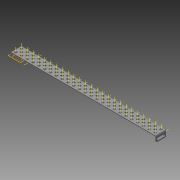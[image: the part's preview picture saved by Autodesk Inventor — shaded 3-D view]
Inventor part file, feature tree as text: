
AUTODESK INVENTOR PART (.ipt)
format: ipt  version: 2015 (Build 190159000, 159)  size: 1,080,320 bytes
history: native  units: in
note: dims shown in document units (in); Inventor stores cm internally (conversion verified against a paired STEP export)
features: other x148, pattern_linear x3, extrude x2, sketch x2, chamfer x1, imported_body x1
ambient origin geometry x8: Origin, YZ Plane, XZ Plane, XY Plane, X Axis, Y Axis, Z Axis, Center Point
bodies: Body1 (feature_tree)
feature tree (157):
  chamfer  "Chamfer2"  Distance=0.5in
  other  "Rail"
  extrude  "right end cut"  Depth=0.5in
  extrude  "length cut"  TaperAngle=0.0deg  [1 undecoded]
  other  "top axis"
  other  "inner axis"
  other  "horiz axis"
  pattern_linear  "top axes"  Count1=3 Spacing1=0.5in
  pattern_linear  "inner axes"  Spacing1=0.0in  [1 undecoded]
  pattern_linear  "horiz axes"  Spacing1=0.0in  [1 undecoded]
  other  "slot plane"
  imported_body  "Base1"
  other  "Work Point1"
  other  "Work Point2"
  other  "Work Axis7"
  other  "Work Axis8"
  other  "Work Axis9"
  other  "Work Axis10"
  other  "Work Axis11"
  other  "Work Axis15"
  other  "Work Axis16"
  other  "Work Axis20"
  other  "Work Axis21"
  other  "Work Axis22"
  other  "Work Axis23"
  other  "Work Axis24"
  other  "Work Point4"
  other  "Work Axis26"
  sketch  "Sketch1"  dims[d8=0.5in d11=0.5in]
  sketch  "Sketch2"  dims[d12=0.1in d13=0.0in d14=-1.0in d15=0.0in d16=1.1811in d18=0.5in d19=0.0in d20=0.0in]
  other  "Work Axis51"
  other  "Work Axis52"
  other  "Work Axis53"
  other  "Work Axis54"
  other  "Work Axis55"
  other  "Work Axis56"
  other  "Work Axis57"
  other  "Work Axis58"
  other  "Work Axis59"
  other  "Work Axis62"
  other  "Work Axis63"
  other  "Work Axis64"
  other  "Work Axis65"
  other  "Work Axis66"
  other  "Work Axis67"
  other  "Work Axis68"
  other  "Work Axis69"
  other  "Work Axis70"
  other  "Work Axis71"
  other  "Work Axis72"
  other  "Work Axis73"
  other  "Work Axis74"
  other  "Work Axis75"
  other  "Work Axis76"
  other  "Work Axis77"
  other  "Work Axis78"
  other  "Work Axis79"
  other  "Work Axis80"
  other  "Work Axis81"
  other  "Work Axis82"
  other  "Work Axis83"
  other  "Work Axis84"
  other  "Work Axis85"
  other  "Work Axis86"
  other  "Work Axis87"
  other  "Work Axis88"
  other  "Work Axis89"
  other  "Work Axis90"
  other  "Work Axis91"
  other  "Work Axis92"
  other  "Work Axis93"
  other  "Work Axis94"
  other  "Work Axis95"
  other  "Work Axis96"
  other  "Work Axis97"
  other  "Work Axis98"
  other  "Work Axis99"
  other  "Work Axis100"
  other  "Work Axis101"
  other  "Work Axis102"
  other  "Work Axis103"
  other  "Work Axis104"
  other  "Work Axis105"
  other  "Work Axis106"
  other  "Work Axis107"
  other  "Work Axis108"
  other  "Work Axis109"
  other  "Work Axis110"
  other  "Work Axis111"
  other  "Work Axis112"
  other  "Work Axis113"
  other  "Work Axis114"
  other  "Work Axis115"
  other  "Work Axis116"
  other  "Work Axis117"
  other  "Work Axis118"
  other  "Work Axis119"
  other  "Work Axis120"
  other  "Work Axis121"
  other  "Work Axis122"
  other  "Work Axis123"
  other  "Work Axis124"
  other  "Work Axis125"
  other  "Work Axis126"
  other  "Work Axis127"
  other  "Work Axis128"
  other  "Work Axis129"
  other  "Work Axis130"
  other  "Work Axis131"
  other  "Work Axis132"
  other  "Work Axis133"
  other  "Work Axis134"
  other  "Work Axis135"
  other  "Work Axis136"
  other  "Work Axis137"
  other  "Work Axis138"
  other  "Work Axis139"
  other  "Work Axis140"
  other  "Work Axis141"
  other  "Work Axis142"
  other  "Work Axis143"
  other  "Work Axis144"
  other  "Work Axis145"
  other  "Work Axis146"
  other  "Work Axis147"
  other  "Work Axis148"
  other  "Work Axis149"
  other  "Work Axis150"
  other  "Work Axis151"
  other  "Work Axis152"
  other  "Work Axis153"
  other  "Work Axis154"
  other  "Work Axis155"
  other  "Work Axis156"
  other  "Work Axis157"
  other  "Work Axis158"
  other  "Work Axis159"
  other  "Work Axis160"
  other  "Work Axis161"
  other  "Work Axis162"
  other  "Work Axis163"
  other  "Work Axis164"
  other  "Work Axis165"
  other  "Work Axis166"
  other  "Work Axis167"
  other  "Work Axis168"
  other  "Work Axis169"
  other  "Work Axis170"
  other  "Work Axis171"
  other  "Work Axis172"
  other  "Work Axis173"
  other  "Work Axis174"
  other  "Work Axis175"
  other  "Work Axis176"
  other  "Work Axis177"
  other  "Work Axis178"
  other  "Work Axis179"
note: 3 required parameter values undecoded (feature->parameter linkage not recoverable at this tier; creation-order binding heuristic only, values carry confidence <= 0.55)
